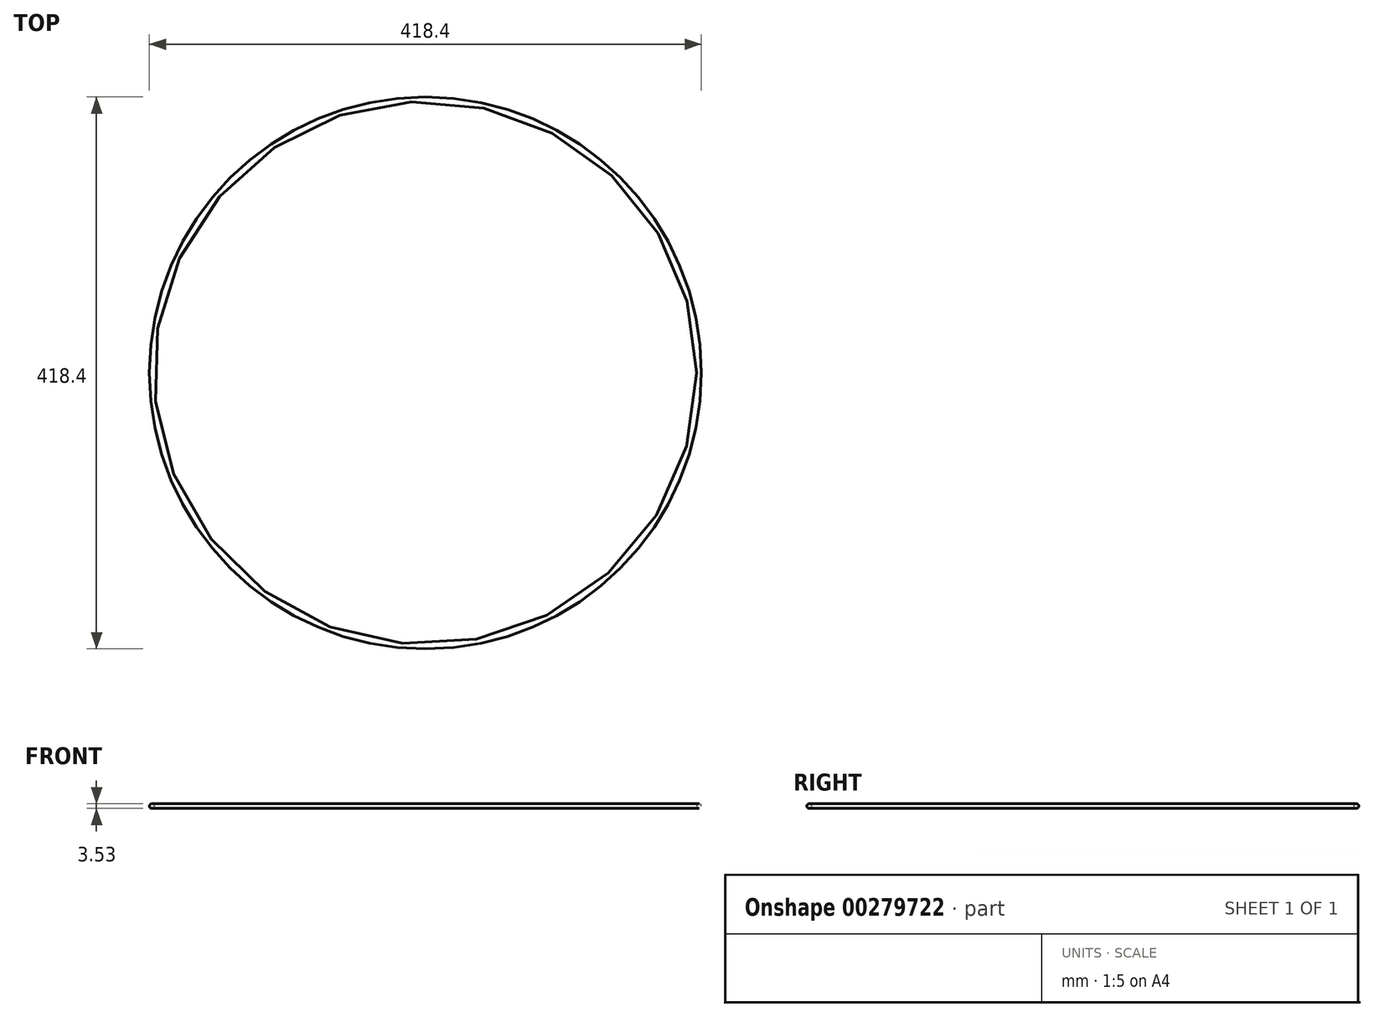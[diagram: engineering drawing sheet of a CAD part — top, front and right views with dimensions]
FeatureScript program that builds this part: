
annotation { "Feature Type Name" : "Feature", "Feature Type Description" : "" }
export const myFeature = defineFeature(function(context is Context, id is Id, definition is map)
    precondition{}
    {
        {
            assignVariable(context, id + "F0", {"name" : "CS", "anyValue" : 0.14});
        }
        {
            var Q0;
            Q0=qCreatedBy(makeId("Top.planeOp"),FACE);
            cPlane(context, id + "F1", {"entities" : qUnion([Q0]), "cplaneType" : CPlaneType.OFFSET, "offset" : (getVariable(context, 'CS')) * mm, "oppositeDirection" : true, "width" : 152.4 * mm, "height" : 152.4 * mm});
        }
        {
            var Q0;
            Q0=qCreatedBy(makeId("Front.planeOp"),FACE);
            var sketch = newSketch(context, id + "F2", { "sketchPlane" : qUnion([Q0])});
            skLineSegment(sketch, "E0", {"start": v(0, 0) * mm, "end": v(0, -3.53) * mm, "construction": true});
            skLineSegment(sketch, "E1", {"start": v(0, -3.53) * mm, "end": v(205.67, -3.53) * mm, "construction": true});
            skLineSegment(sketch, "E2", {"start": v(205.67, 0) * mm, "end": v(0, 0) * mm, "construction": true});
            skCircle(sketch, "E3", {"center": v(207.43, -1.77) * mm, "radius": 1.77 * mm});
            skLineSegment(sketch, "E4", {"start": v(205.67, -1.77) * mm, "end": v(207.43, -1.77) * mm, "construction": true});
            skLineSegment(sketch, "E5", {"start": v(205.67, 0) * mm, "end": v(205.67, -1.77) * mm, "construction": true});
            skLineSegment(sketch, "E6", {"start": v(205.67, -3.53) * mm, "end": v(205.67, -1.77) * mm, "construction": true});
            skSolve(sketch);
        }
        {
            var Q0;
            Q0 = qSketchRegion(id + "F2", true);
            var Q1;
            Q1=sQuery(id+"F2.wireOp",EDGE,"E0");
            revolve(context, id + "F3", {"entities" : qUnion([Q0]), "axis" : qUnion([Q1]), "revolveType" : RevolveType.FULL});
        }
    });
